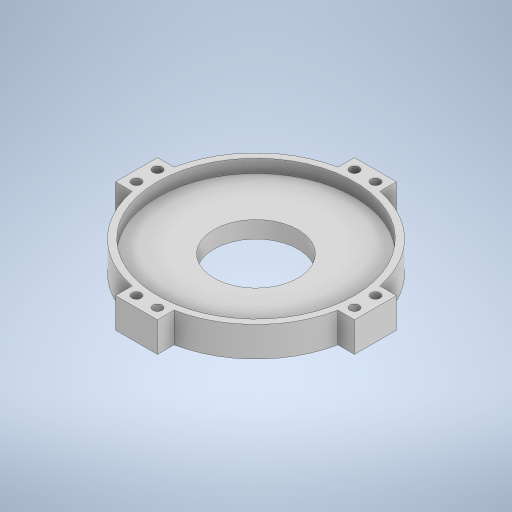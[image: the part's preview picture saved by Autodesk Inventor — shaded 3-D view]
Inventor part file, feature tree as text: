
AUTODESK INVENTOR PART (.ipt)
format: ipt  version: 2023 (Build 270158000, 158)  size: 332,288 bytes
history: native  units: in
note: dims shown in document units (in); Inventor stores cm internally (conversion verified against a paired STEP export)
features: extrude x4, sketch x4
ambient origin geometry x8: Origin, YZ Plane, XZ Plane, XY Plane, X Axis, Y Axis, Z Axis, Center Point
bodies: Solid1 (feature_tree)
feature tree (8):
  extrude  "Extrusion1"  Depth=1.6in
  extrude  "Extrusion2"  Depth=0.571in
  extrude  "Extrusion3"  Depth=0.25in
  extrude  "Extrusion4"  Depth=0.8in
  sketch  "Sketch1"  dims[d0=4.0in d1=1.6in]
  sketch  "Sketch2"  dims[d2=0.571in d3=0.0in d4=3.75in]
  sketch  "Sketch3"  dims[d5=0.25in d6=0.0in d7=0.4in]
  sketch  "Sketch4"  dims[d8=0.4in d9=0.8in d10=0.4in d11=0.4in d12=0.4in d13=0.8in d14=0.4in d15=0.4in d16=0.4in d17=0.8in d18=0.4in d19=0.4in d20=0.4in d21=0.4in d22=0.8in d23=0.4in d24=0.25in d25=0.0in d26=0.2in d27=0.2in d28=0.4in d29=0.2in d30=0.2in d31=0.4in d32=0.2in d33=0.2in d34=0.4in d35=0.2in d36=0.2in d37=0.4in d38=0.177in d39=0.177in d40=0.177in d41=0.177in d42=0.177in d43=0.177in d44=0.177in d45=1.0in d46=0.0in]
